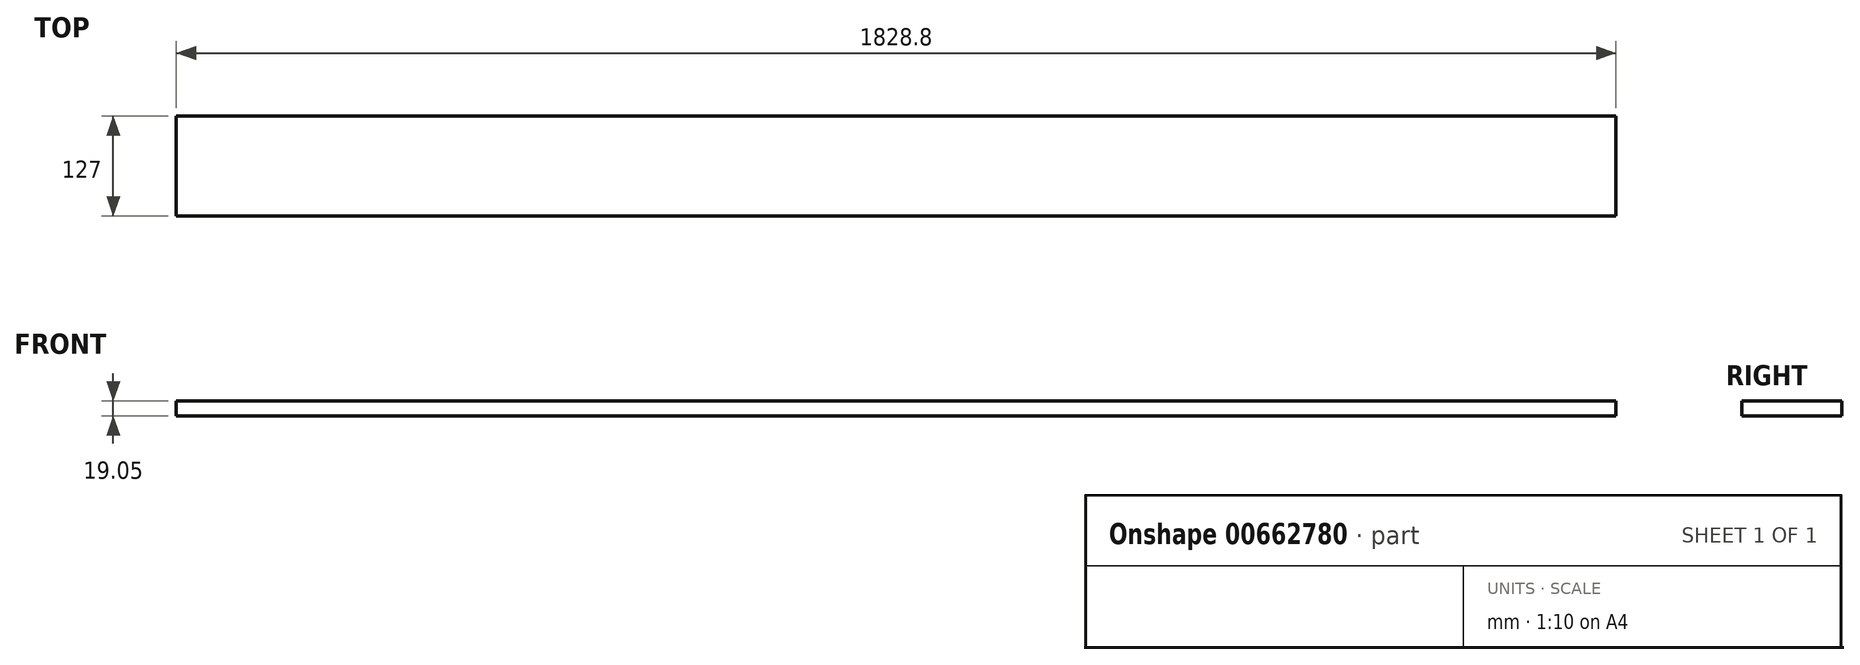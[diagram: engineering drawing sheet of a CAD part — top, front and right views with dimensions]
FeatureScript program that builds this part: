
annotation { "Feature Type Name" : "Feature", "Feature Type Description" : "" }
export const myFeature = defineFeature(function(context is Context, id is Id, definition is map)
    precondition{}
    {
        {
            var Q0;
            Q0=qCreatedBy(makeId("Top.planeOp"),FACE);
            var sketch = newSketch(context, id + "F0", { "sketchPlane" : qUnion([Q0])});
            skLineSegment(sketch, "E0.bottom", {"start": v(751.43, -13.87) * mm, "end": v(-1077.37, -13.87) * mm});
            skLineSegment(sketch, "E0.top", {"start": v(751.43, 113.13) * mm, "end": v(-1077.37, 113.13) * mm});
            skLineSegment(sketch, "E0.left", {"start": v(751.43, -13.87) * mm, "end": v(751.43, 113.13) * mm});
            skLineSegment(sketch, "E0.right", {"start": v(-1077.37, -13.87) * mm, "end": v(-1077.37, 113.13) * mm});
            skPoint(sketch, "E0.middle", {"position": v(-162.97, 49.63) * mm});
            skSolve(sketch);
        }
        {
            var Q0;
            Q0=makeQuery(id+"F0.imprint","IMPRINT",FACE,{"disambiguationData":[TD([[makeQuery(id+"F0.imprint","IMPRINT",EDGE,{"derivedFrom":sQuery(id+"F0.wireOp",EDGE,"E0.bottom")}),-1.0]])]});
            extrude(context, id + "F1", {"entities" : qUnion([Q0]), "depth" : 19.05 * mm, "offsetDistance" : 25.4 * mm});
        }
    });
